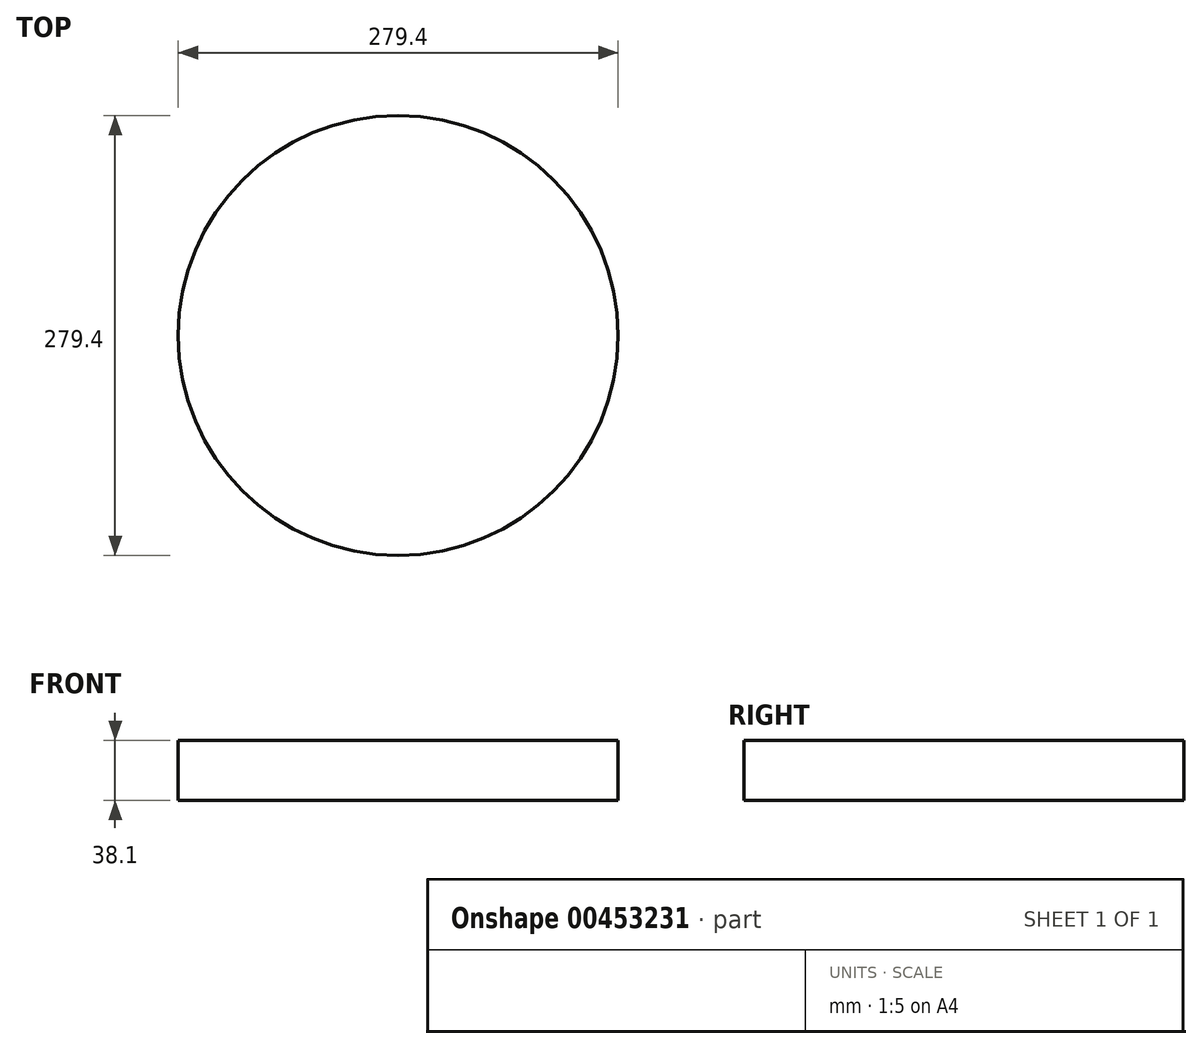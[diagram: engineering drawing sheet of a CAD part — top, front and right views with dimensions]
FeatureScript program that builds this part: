
annotation { "Feature Type Name" : "Feature", "Feature Type Description" : "" }
export const myFeature = defineFeature(function(context is Context, id is Id, definition is map)
    precondition{}
    {
        {
            var Q0;
            Q0=qCreatedBy(makeId("Top.planeOp"),FACE);
            var sketch = newSketch(context, id + "F0", { "sketchPlane" : qUnion([Q0])});
            skCircle(sketch, "E0", {"center": v(0, 0) * mm, "radius": 139.7 * mm});
            skSolve(sketch);
        }
        {
            var Q0;
            Q0=makeQuery(id+"F0.imprint","IMPRINT",FACE,{"disambiguationData":[TD([[makeQuery(id+"F0.imprint","IMPRINT",EDGE,{"derivedFrom":sQuery(id+"F0.wireOp",EDGE,"E0")}),1.0]])]});
            extrude(context, id + "F1", {"entities" : qUnion([Q0]), "depth" : 38.1 * mm});
        }
        {
            var Q0;
            Q0=makeQuery(id+"F1.opExtrude","SWEPT_BODY",BODY,{"disambiguationData":[OSD([sQuery(id+"F0.wireOp",EDGE,"E0")])]});
            var Q1;
            Q1=makeQuery(id+"F1.opExtrude","CAP_EDGE",EDGE,{"disambiguationData":[OSD([sQuery(id+"F0.wireOp",EDGE,"E0")])],"isStart":false});
            circularPattern(context, id + "F2", {"entities" : qUnion([Q0]), "axis" : qUnion([Q1]), "angle" : 360 * degree, "instanceCount" : 7, "equalSpace" : true, "isCentered" : true});
        }
    });
